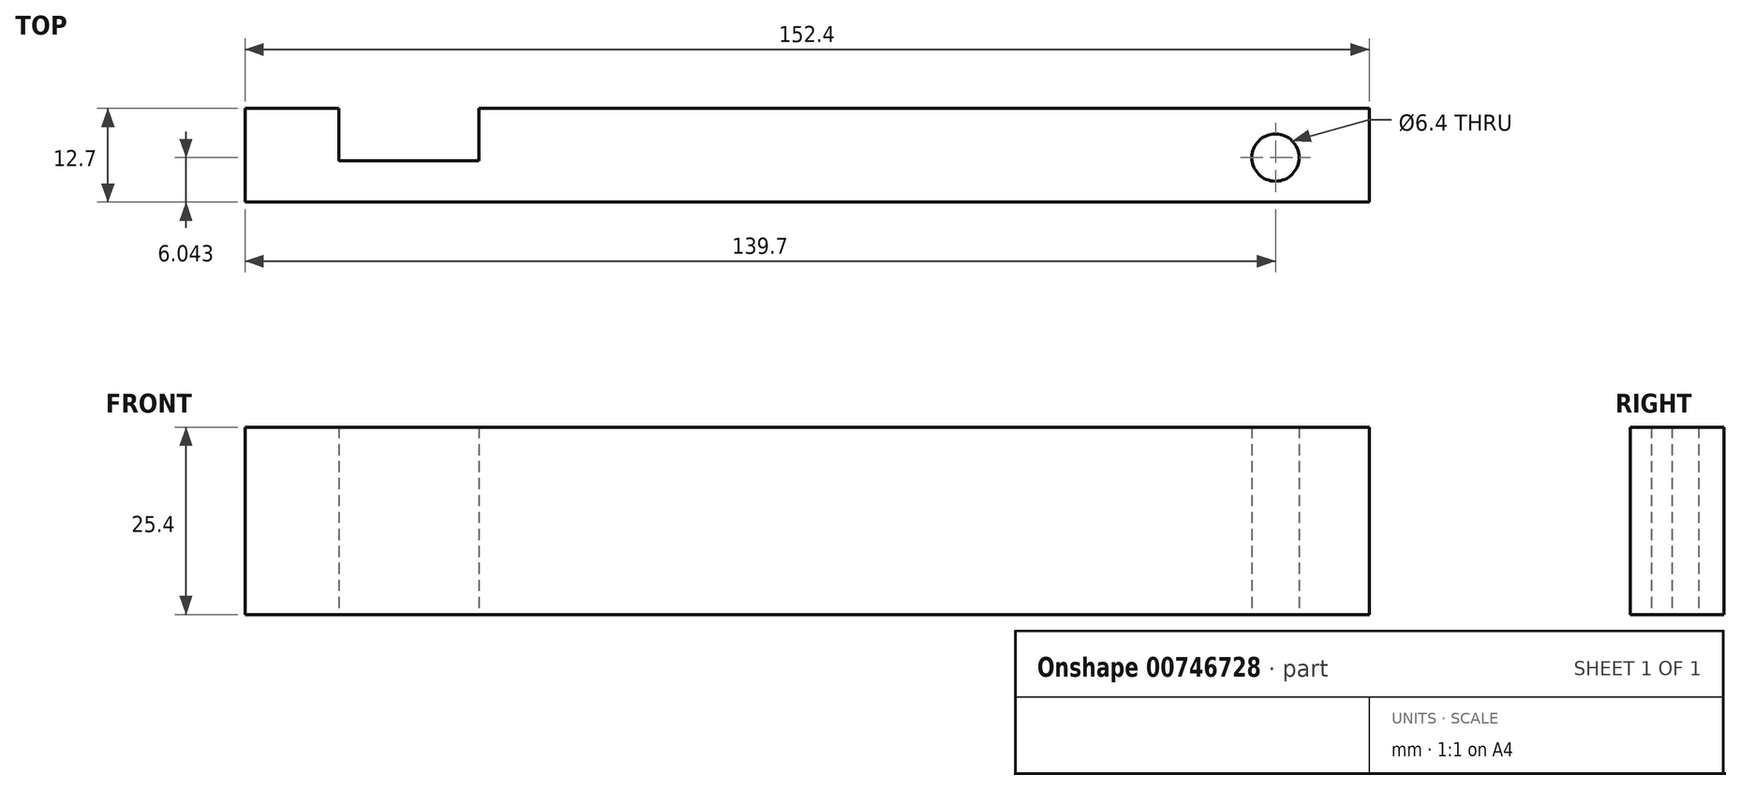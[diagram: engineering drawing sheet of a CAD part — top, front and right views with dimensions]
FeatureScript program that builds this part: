
annotation { "Feature Type Name" : "Feature", "Feature Type Description" : "" }
export const myFeature = defineFeature(function(context is Context, id is Id, definition is map)
    precondition{}
    {
        {
            var Q0;
            Q0=qCreatedBy(makeId("Top.planeOp"),FACE);
            var sketch = newSketch(context, id + "F0", { "sketchPlane" : qUnion([Q0])});
            skLineSegment(sketch, "E0.bottom", {"start": v(0, 57.34) * mm, "end": v(-152.4, 57.34) * mm});
            skLineSegment(sketch, "E0.top", {"start": v(0, 70.04) * mm, "end": v(-152.4, 70.04) * mm});
            skLineSegment(sketch, "E0.left", {"start": v(0, 57.34) * mm, "end": v(0, 70.04) * mm});
            skLineSegment(sketch, "E0.right", {"start": v(-152.4, 57.34) * mm, "end": v(-152.4, 70.04) * mm});
            skPoint(sketch, "E0.middle", {"position": v(-76.2, 63.7) * mm});
            skSolve(sketch);
        }
        {
            var Q0;
            Q0=makeQuery(id+"F0.imprint","IMPRINT",FACE,{"disambiguationData":[TD([[makeQuery(id+"F0.imprint","IMPRINT",EDGE,{"derivedFrom":sQuery(id+"F0.wireOp",EDGE,"E0.bottom")}),-1.0]])]});
            var sketch = newSketch(context, id + "F1", { "sketchPlane" : qUnion([Q0])});
            skCircle(sketch, "E1", {"center": v(-12.7, 63.38) * mm, "radius": 3.2 * mm});
            skSolve(sketch);
        }
        {
            var Q0;
            Q0=makeQuery(id+"F1.imprint","IMPRINT",FACE,{"disambiguationData":[TD([[makeQuery(id+"F1.imprint","IMPRINT",EDGE,{"derivedFrom":sQuery(id+"F1.wireOp",EDGE,"E1")}),-1.0]])]});
            var sketch = newSketch(context, id + "F2", { "sketchPlane" : qUnion([Q0])});
            skLineSegment(sketch, "E2.bottom", {"start": v(-139.7, 70.44) * mm, "end": v(-120.65, 70.44) * mm});
            skLineSegment(sketch, "E2.top", {"start": v(-139.7, 62.98) * mm, "end": v(-120.65, 62.98) * mm});
            skLineSegment(sketch, "E2.left", {"start": v(-139.7, 70.44) * mm, "end": v(-139.7, 62.98) * mm});
            skLineSegment(sketch, "E2.right", {"start": v(-120.65, 70.44) * mm, "end": v(-120.65, 62.98) * mm});
            skSolve(sketch);
        }
        {
            var Q0;
            {var subQ1=sQuery(id+"F2.wireOp",EDGE,"E2.top");Q0=makeQuery(id+"F2.imprint","IMPRINT",FACE,{"disambiguationData":[TD([[makeQuery(id+"F2.imprint","IMPRINT",EDGE,{"derivedFrom":subQ1}),-1.0]])]});}
            extrude(context, id + "F3", {"entities" : qUnion([Q0]), "depth" : 25.4 * mm, "offsetDistance" : 25.4 * mm});
        }
    });
